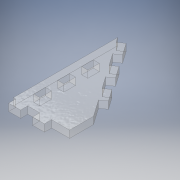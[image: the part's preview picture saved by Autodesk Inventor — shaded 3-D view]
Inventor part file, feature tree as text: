
AUTODESK INVENTOR PART (.ipt)
format: ipt  version: 2019 (Build 230136000, 136)  size: 172,032 bytes
history: native  units: mm
features: extrude x1, sketch x1
ambient origin geometry x8: Origin, YZ Plane, XZ Plane, XY Plane, X Axis, Y Axis, Z Axis, Center Point
bodies: Body1 (feature_tree)
feature tree (2):
  extrude  "Extrusion2"  Depth=10.0mm
  sketch  "Sketch2"  dims[d9=20.0mm d19=10.0mm d20=6.0mm d21=2.0mm d31=6.0mm d32=0.0mm d41=9.599311mm d42=6.0mm d43=30.0mm d45=24.0mm d46=10.0mm d48=10.0mm d50=5.0mm d51=12.0mm d52=10.0mm d53=6.0mm d54=10.0mm d55=47.0mm d56=10.0mm d57=5.1mm d58=9.7mm d59=30.0mm d61=20.0mm d62=10.0mm d64=10.0mm d66=6.0mm d67=6.0mm]
